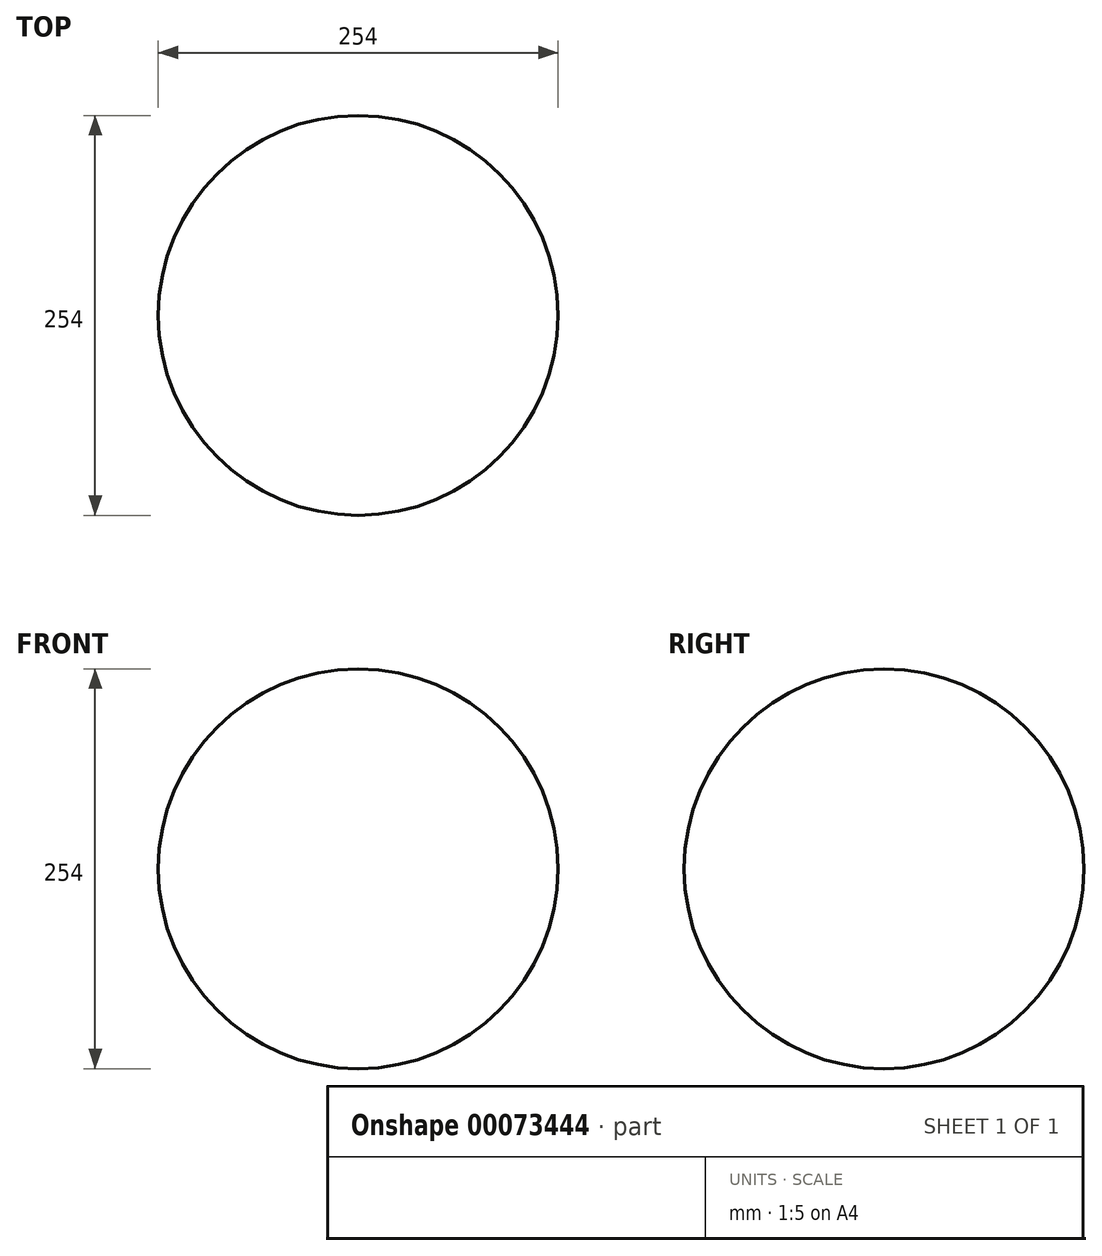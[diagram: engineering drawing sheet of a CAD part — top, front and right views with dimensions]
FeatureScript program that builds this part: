
annotation { "Feature Type Name" : "Feature", "Feature Type Description" : "" }
export const myFeature = defineFeature(function(context is Context, id is Id, definition is map)
    precondition{}
    {
        {
            var Q0;
            Q0=qCreatedBy(makeId("Top.planeOp"),FACE);
            var sketch = newSketch(context, id + "F0", { "sketchPlane" : qUnion([Q0])});
            skLineSegment(sketch, "E0", {"start": v(0, 0) * mm, "end": v(0, -127) * mm});
            skArc(sketch, "E1", {"start": v(0, -127) * mm, "mid": v(-127, 0) * mm, "end": v(0, 127) * mm});
            skLineSegment(sketch, "E2", {"start": v(0, 127) * mm, "end": v(0, 0) * mm});
            skSolve(sketch);
        }
        {
            var Q0;
            Q0=makeQuery(id+"F0.imprint","IMPRINT",FACE,{"disambiguationData":[TD([[makeQuery(id+"F0.imprint","IMPRINT",EDGE,{"derivedFrom":sQuery(id+"F0.wireOp",EDGE,"E0")}),-1.0]])]});
            var Q1;
            Q1=sQuery(id+"F0.wireOp",EDGE,"E0");
            revolve(context, id + "F1", {"entities" : qUnion([Q0]), "axis" : qUnion([Q1]), "revolveType" : RevolveType.FULL});
        }
    });
